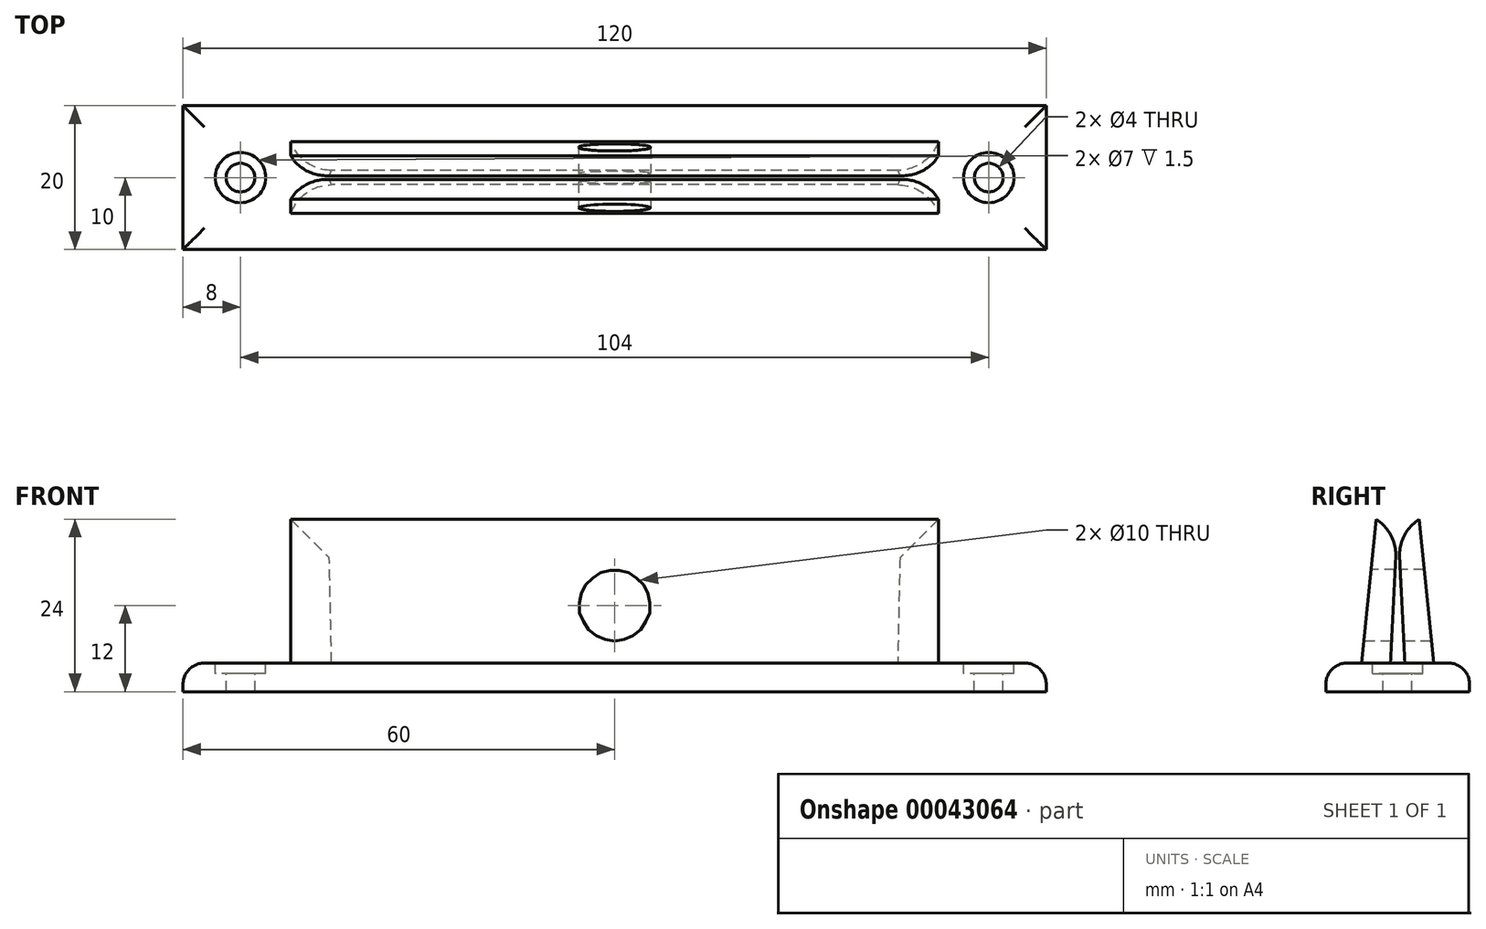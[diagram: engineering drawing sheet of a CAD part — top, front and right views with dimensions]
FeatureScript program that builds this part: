
annotation { "Feature Type Name" : "Feature", "Feature Type Description" : "" }
export const myFeature = defineFeature(function(context is Context, id is Id, definition is map)
    precondition{}
    {
        {
            var Q0;
            Q0=qCreatedBy(makeId("Top.planeOp"),FACE);
            var sketch = newSketch(context, id + "F0", { "sketchPlane" : qUnion([Q0])});
            skLineSegment(sketch, "E0.rect.bottom", {"start": v(60, -10) * mm, "end": v(-60, -10) * mm});
            skLineSegment(sketch, "E0.rect.top", {"start": v(60, 10) * mm, "end": v(-60, 10) * mm});
            skLineSegment(sketch, "E0.rect.left", {"start": v(60, -10) * mm, "end": v(60, 10) * mm});
            skLineSegment(sketch, "E0.rect.right", {"start": v(-60, -10) * mm, "end": v(-60, 10) * mm});
            skPoint(sketch, "E0.rect.middle", {"position": v(0, 0) * mm});
            skCircle(sketch, "E1", {"center": v(-52, 0) * mm, "radius": 2 * mm});
            skCircle(sketch, "E2", {"center": v(52, 0) * mm, "radius": 2 * mm});
            skCircle(sketch, "E3", {"center": v(-52, 0) * mm, "radius": 3.5 * mm});
            skCircle(sketch, "E4", {"center": v(52, 0) * mm, "radius": 3.5 * mm});
            skSolve(sketch);
        }
        {
            var Q0;
            Q0=makeQuery(id+"F0.imprint","IMPRINT",FACE,{"disambiguationData":[TD([[makeQuery(id+"F0.imprint","IMPRINT",EDGE,{"derivedFrom":sQuery(id+"F0.wireOp",EDGE,"E0.rect.bottom")}),-1.0]])]});
            var Q1;
            Q1=makeQuery(id+"F0.imprint","IMPRINT",FACE,{"disambiguationData":[TD([[makeQuery(id+"F0.imprint","IMPRINT",EDGE,{"derivedFrom":sQuery(id+"F0.wireOp",EDGE,"E2")}),-1.0]])]});
            var Q2;
            Q2=makeQuery(id+"F0.imprint","IMPRINT",FACE,{"disambiguationData":[TD([[makeQuery(id+"F0.imprint","IMPRINT",EDGE,{"derivedFrom":sQuery(id+"F0.wireOp",EDGE,"E1")}),-1.0]])]});
            extrude(context, id + "F1", {"entities" : qUnion([Q0, Q1, Q2]), "oppositeDirection" : true, "depth" : 4 * mm});
        }
        {
            var Q0;
            Q0=makeQuery(id+"F0.imprint","IMPRINT",FACE,{"disambiguationData":[TD([[makeQuery(id+"F0.imprint","IMPRINT",EDGE,{"derivedFrom":sQuery(id+"F0.wireOp",EDGE,"E2")}),-1.0]])]});
            var Q1;
            Q1=makeQuery(id+"F0.imprint","IMPRINT",FACE,{"disambiguationData":[TD([[makeQuery(id+"F0.imprint","IMPRINT",EDGE,{"derivedFrom":sQuery(id+"F0.wireOp",EDGE,"E1")}),-1.0]])]});
            extrude(context, id + "F2", {"entities" : qUnion([Q0, Q1]), "operationType" : NewBodyOperationType.REMOVE, "oppositeDirection" : true, "depth" : 1.5 * mm});
        }
        {
            var Q0;
            Q0=makeQuery(id+"F1.opExtrude","CAP_EDGE",EDGE,{"disambiguationData":[OSD([sQuery(id+"F0.wireOp",EDGE,"E0.rect.right")])],"isStart":true});
            var Q1;
            Q1=makeQuery(id+"F1.opExtrude","CAP_EDGE",EDGE,{"disambiguationData":[OSD([sQuery(id+"F0.wireOp",EDGE,"E0.rect.bottom")])],"isStart":true});
            var Q2;
            Q2=makeQuery(id+"F1.opExtrude","CAP_EDGE",EDGE,{"disambiguationData":[OSD([sQuery(id+"F0.wireOp",EDGE,"E0.rect.top")])],"isStart":true});
            var Q3;
            Q3=makeQuery(id+"F1.opExtrude","CAP_EDGE",EDGE,{"disambiguationData":[OSD([sQuery(id+"F0.wireOp",EDGE,"E0.rect.left")])],"isStart":true});
            fillet(context, id + "F3", {"entities" : qUnion([Q0, Q1, Q2, Q3]), "radius" : 3 * mm, "tangentPropagation" : true, "allowEdgeOverflow" : false});
        }
        {
            var Q0;
            Q0=qCreatedBy(makeId("Right.planeOp"),FACE);
            var sketch = newSketch(context, id + "F4", { "sketchPlane" : qUnion([Q0])});
            skLineSegment(sketch, "E5", {"start": v(-3, 20) * mm, "end": v(-5, 0) * mm});
            skLineSegment(sketch, "E6", {"start": v(-5, 0) * mm, "end": v(-1, 0) * mm});
            skLineSegment(sketch, "E7", {"start": v(0, 20) * mm, "end": v(-1, 0) * mm});
            skLineSegment(sketch, "E8", {"start": v(-3, 20) * mm, "end": v(0, 20) * mm});
            skLineSegment(sketch, "E9.MirrorCS", {"start": v(0, 20) * mm, "end": v(1, 0) * mm});
            skLineSegment(sketch, "E10.MirrorCS", {"start": v(5, 0) * mm, "end": v(1, 0) * mm});
            skLineSegment(sketch, "E11.MirrorCS", {"start": v(3, 20) * mm, "end": v(5, 0) * mm});
            skLineSegment(sketch, "E12.MirrorCS", {"start": v(3, 20) * mm, "end": v(0, 20) * mm});
            skSolve(sketch);
        }
        {
            var Q0;
            Q0 = qSketchRegion(id + "F4", true);
            extrude(context, id + "F5", {"entities" : qUnion([Q0]), "endBound" : BoundingType.SYMMETRIC, "depth" : 90 * mm});
        }
        {
            var Q0;
            {var subQ0=sQuery(id+"F4.wireOp",EDGE,"E7");var subQ1=sQuery(id+"F4.wireOp",EDGE,"E8");Q0=makeQuery(id+"F5.opExtrude","SWEPT_EDGE",EDGE,{"disambiguationData":[OSD([subQ0,subQ1,sQuery(id+"F4.wireOp",EDGE,"E9.MirrorCS"),sQuery(id+"F4.wireOp",EDGE,"E12.MirrorCS")]),ownerDisambiguation([makeQuery(id+"F5.opExtrude","SWEPT_BODY",BODY,{"disambiguationData":[OSD([sQuery(id+"F4.wireOp",EDGE,"E5"),sQuery(id+"F4.wireOp",EDGE,"E6"),subQ0,subQ1])]})])]});}
            var Q1;
            Q1=makeQuery(id+"F5.opExtrude","CAP_EDGE",EDGE,{"disambiguationData":[OSD([sQuery(id+"F4.wireOp",EDGE,"E7")])],"isStart":false});
            var Q2;
            Q2=makeQuery(id+"F5.opExtrude","CAP_EDGE",EDGE,{"disambiguationData":[OSD([sQuery(id+"F4.wireOp",EDGE,"E7")])],"isStart":true});
            var Q3;
            {var subQ0=sQuery(id+"F4.wireOp",EDGE,"E9.MirrorCS");var subQ1=sQuery(id+"F4.wireOp",EDGE,"E12.MirrorCS");Q3=makeQuery(id+"F5.opExtrude","SWEPT_EDGE",EDGE,{"disambiguationData":[OSD([sQuery(id+"F4.wireOp",EDGE,"E7"),sQuery(id+"F4.wireOp",EDGE,"E8"),subQ0,subQ1]),ownerDisambiguation([makeQuery(id+"F5.opExtrude","SWEPT_BODY",BODY,{"disambiguationData":[OSD([subQ0,sQuery(id+"F4.wireOp",EDGE,"E10.MirrorCS"),sQuery(id+"F4.wireOp",EDGE,"E11.MirrorCS"),subQ1])]})])]});}
            var Q4;
            Q4=makeQuery(id+"F5.opExtrude","CAP_EDGE",EDGE,{"disambiguationData":[OSD([sQuery(id+"F4.wireOp",EDGE,"E9.MirrorCS")])],"isStart":true});
            var Q5;
            Q5=makeQuery(id+"F5.opExtrude","CAP_EDGE",EDGE,{"disambiguationData":[OSD([sQuery(id+"F4.wireOp",EDGE,"E9.MirrorCS")])],"isStart":false});
            fillet(context, id + "F6", {"entities" : qUnion([Q0, Q1, Q2, Q3, Q4, Q5]), "radius" : 6 * mm, "tangentPropagation" : true, "allowEdgeOverflow" : false});
        }
        {
            var Q0;
            Q0=qCreatedBy(makeId("Front.planeOp"),FACE);
            var sketch = newSketch(context, id + "F7", { "sketchPlane" : qUnion([Q0])});
            skCircle(sketch, "E13", {"center": v(0, 8) * mm, "radius": 5 * mm});
            skSolve(sketch);
        }
        {
            var Q0;
            Q0 = qSketchRegion(id + "F7", true);
            extrude(context, id + "F8", {"entities" : qUnion([Q0]), "operationType" : NewBodyOperationType.REMOVE, "endBound" : BoundingType.SYMMETRIC, "oppositeDirection" : true, "depth" : 20 * mm});
        }
    });
